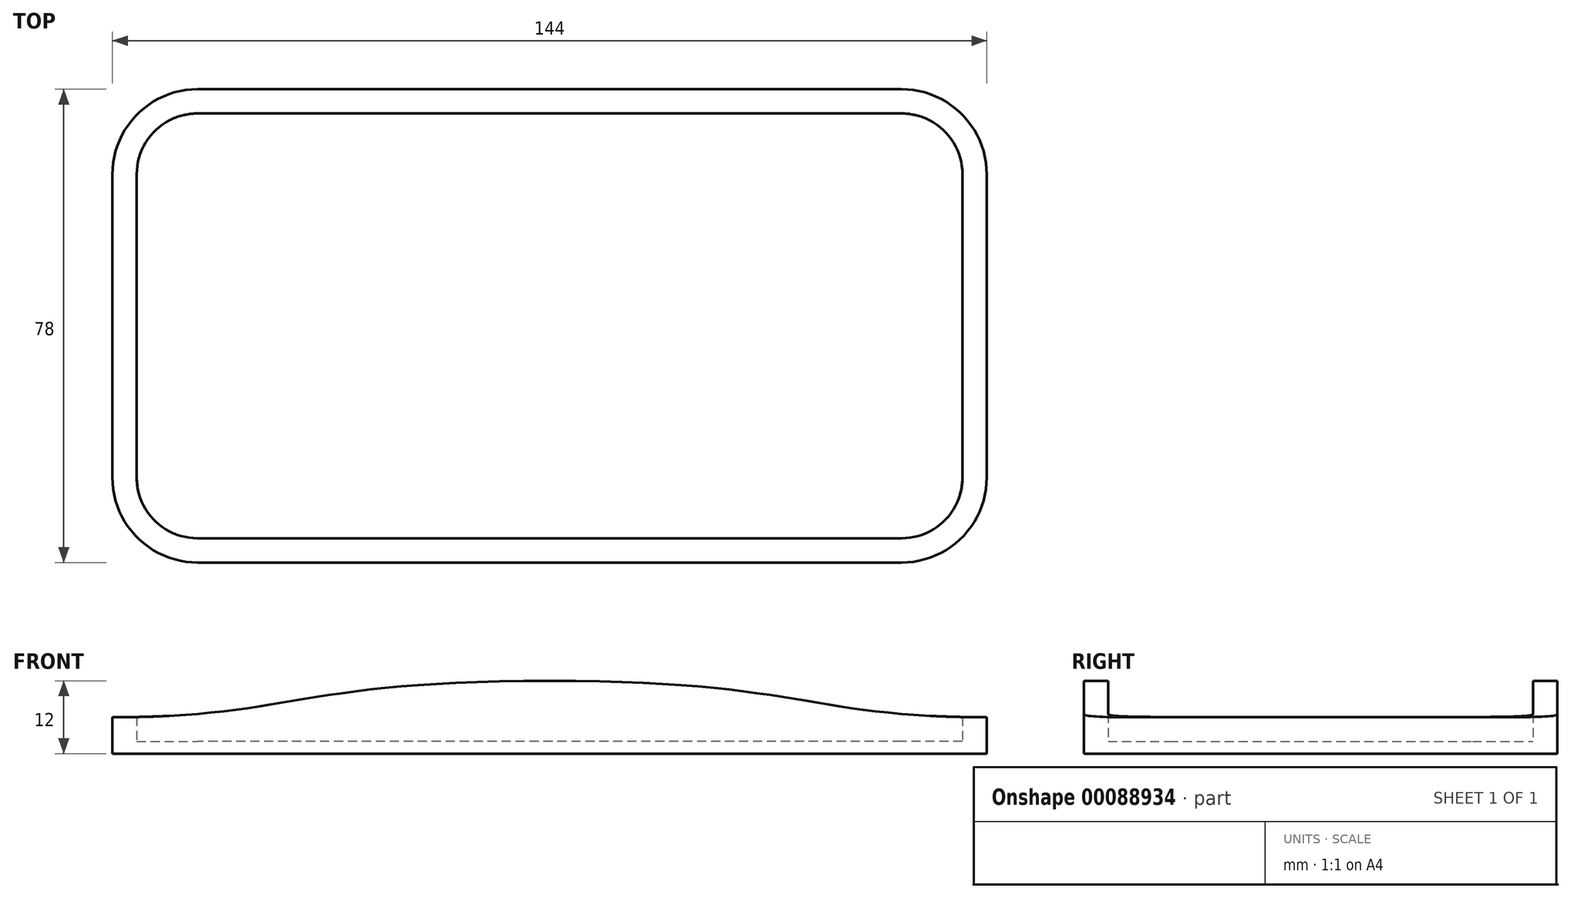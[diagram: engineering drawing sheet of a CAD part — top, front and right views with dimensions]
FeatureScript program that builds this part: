
annotation { "Feature Type Name" : "Feature", "Feature Type Description" : "" }
export const myFeature = defineFeature(function(context is Context, id is Id, definition is map)
    precondition{}
    {
        {
            var Q0;
            Q0=qCreatedBy(makeId("Top.planeOp"),FACE);
            var sketch = newSketch(context, id + "F0", { "sketchPlane" : qUnion([Q0])});
            skLineSegment(sketch, "E0.bottom", {"start": v(58, -35) * mm, "end": v(-58, -35) * mm});
            skLineSegment(sketch, "E0.top", {"start": v(58, 35) * mm, "end": v(-58, 35) * mm});
            skLineSegment(sketch, "E0.left", {"start": v(68, -25) * mm, "end": v(68, 25) * mm});
            skLineSegment(sketch, "E0.right", {"start": v(-68, -25) * mm, "end": v(-68, 25) * mm});
            skPoint(sketch, "E0.middle", {"position": v(0, 0) * mm});
            skPoint(sketch, "E1.visualSharp", {"position": v(-68, 35) * mm});
            skArc(sketch, "E1.filletArc", {"start": v(-58, 35) * mm, "mid": v(-65.07, 32.07) * mm, "end": v(-68, 25) * mm});
            skPoint(sketch, "E2.visualSharp", {"position": v(68, 35) * mm});
            skArc(sketch, "E2.filletArc", {"start": v(68, 25) * mm, "mid": v(65.07, 32.07) * mm, "end": v(58, 35) * mm});
            skPoint(sketch, "E3.visualSharp", {"position": v(68, -35) * mm});
            skArc(sketch, "E3.filletArc", {"start": v(58, -35) * mm, "mid": v(65.07, -32.07) * mm, "end": v(68, -25) * mm});
            skPoint(sketch, "E4.visualSharp", {"position": v(-68, -35) * mm});
            skArc(sketch, "E4.filletArc", {"start": v(-68, -25) * mm, "mid": v(-65.07, -32.07) * mm, "end": v(-58, -35) * mm});
            skArc(sketch, "E5.0", {"start": v(72, 25) * mm, "mid": v(67.9, 34.9) * mm, "end": v(58, 39) * mm});
            skLineSegment(sketch, "E5.1", {"start": v(72, -25) * mm, "end": v(72, 25) * mm});
            skLineSegment(sketch, "E5.2", {"start": v(58, 39) * mm, "end": v(-58, 39) * mm});
            skArc(sketch, "E5.3", {"start": v(58, -39) * mm, "mid": v(67.9, -34.9) * mm, "end": v(72, -25) * mm});
            skArc(sketch, "E5.4", {"start": v(-58, 39) * mm, "mid": v(-67.9, 34.9) * mm, "end": v(-72, 25) * mm});
            skLineSegment(sketch, "E5.5", {"start": v(-72, -25) * mm, "end": v(-72, 25) * mm});
            skArc(sketch, "E5.6", {"start": v(-72, -25) * mm, "mid": v(-67.9, -34.9) * mm, "end": v(-58, -39) * mm});
            skLineSegment(sketch, "E5.7", {"start": v(58, -39) * mm, "end": v(-58, -39) * mm});
            skSolve(sketch);
        }
        {
            var Q0;
            Q0=makeQuery(id+"F0.imprint","IMPRINT",FACE,{"disambiguationData":[TD([[makeQuery(id+"F0.imprint","IMPRINT",EDGE,{"derivedFrom":sQuery(id+"F0.wireOp",EDGE,"E0.bottom")}),-1.0]])]});
            extrude(context, id + "F1", {"entities" : qUnion([Q0]), "depth" : 2 * mm});
        }
        {
            var Q0;
            Q0=makeQuery(id+"F0.imprint","IMPRINT",FACE,{"disambiguationData":[TD([[makeQuery(id+"F0.imprint","IMPRINT",EDGE,{"derivedFrom":sQuery(id+"F0.wireOp",EDGE,"E0.bottom")}),1.0]])]});
            extrude(context, id + "F2", {"entities" : qUnion([Q0]), "operationType" : NewBodyOperationType.ADD, "depth" : 12 * mm});
        }
        {
            var Q0;
            Q0=qCreatedBy(makeId("Front.planeOp"),FACE);
            var sketch = newSketch(context, id + "F3", { "sketchPlane" : qUnion([Q0])});
            skLineSegment(sketch, "E6.0", {"start": v(72, 0) * mm, "end": v(-72, 0) * mm});
            skLineSegment(sketch, "E7.0", {"start": v(72, 12) * mm, "end": v(72, 0) * mm});
            skLineSegment(sketch, "E8.0", {"start": v(-72, 12) * mm, "end": v(-72, 0) * mm});
            skLineSegment(sketch, "E9.0", {"start": v(58, 12) * mm, "end": v(-58, 12) * mm});
            skFitSpline(sketch, "E10", {"points": [v(72, 6) * mm, v(0, 12) * mm], "startDerivative": vector(-89.2, 0) * mm, "endDerivative": vector(-124.8, 0) * mm});
            skLineSegment(sketch, "E11", {"start": v(0, 0) * mm, "end": v(0, 12) * mm, "construction": true});
            skFitSpline(sketch, "E12.MirrorCS", {"points": [v(-72, 6) * mm, v(0, 12) * mm], "startDerivative": vector(89.2, 0) * mm, "endDerivative": vector(124.8, 0) * mm});
            skPoint(sketch, "E13.orphan", {"position": v(58, 0) * mm});
            skPoint(sketch, "E14.orphan", {"position": v(-58, 0) * mm});
            skSolve(sketch);
        }
        {
            var Q0;
            {var subQ1=sQuery(id+"F3.wireOp",EDGE,"E6.0");Q0=makeQuery(id+"F3.imprint","IMPRINT",FACE,{"disambiguationData":[TD([[makeQuery(id+"F3.imprint","IMPRINT",EDGE,{"derivedFrom":subQ1}),-1.0]])]});}
            extrude(context, id + "F4", {"entities" : qUnion([Q0]), "operationType" : NewBodyOperationType.INTERSECT, "endBound" : BoundingType.SYMMETRIC, "depth" : 99 * mm});
        }
    });
